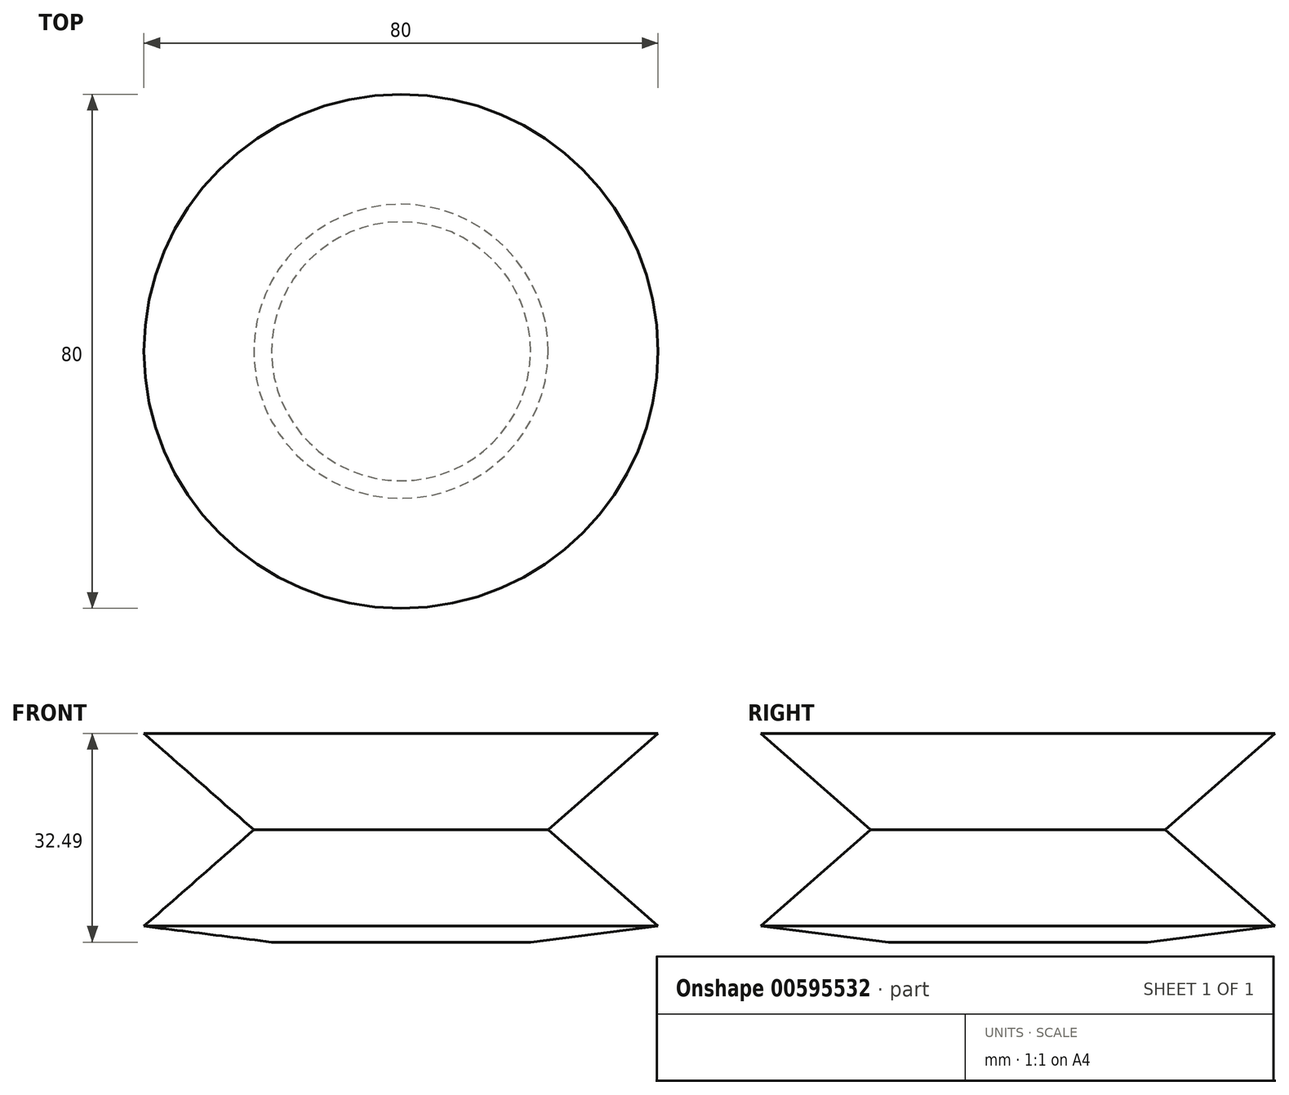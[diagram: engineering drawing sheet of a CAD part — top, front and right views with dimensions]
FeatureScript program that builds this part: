
annotation { "Feature Type Name" : "Feature", "Feature Type Description" : "" }
export const myFeature = defineFeature(function(context is Context, id is Id, definition is map)
    precondition{}
    {
        {
            var Q0;
            Q0=qCreatedBy(makeId("Front.planeOp"),FACE);
            var sketch = newSketch(context, id + "F0", { "sketchPlane" : qUnion([Q0])});
            skLineSegment(sketch, "E0", {"start": v(0, 0) * mm, "end": v(0, 32.49) * mm});
            skLineSegment(sketch, "E1", {"start": v(0, 32.49) * mm, "end": v(40, 32.49) * mm});
            skLineSegment(sketch, "E2", {"start": v(40, 32.49) * mm, "end": v(22.9, 17.49) * mm});
            skLineSegment(sketch, "E3", {"start": v(22.9, 17.49) * mm, "end": v(40, 2.49) * mm});
            skLineSegment(sketch, "E4", {"start": v(40, 2.49) * mm, "end": v(20.16, 0) * mm});
            skLineSegment(sketch, "E5", {"start": v(20.16, 0) * mm, "end": v(0, 0) * mm});
            skSolve(sketch);
        }
        {
            var Q0;
            Q0=makeQuery(id+"F0.imprint","IMPRINT",FACE,{"disambiguationData":[TD([[makeQuery(id+"F0.imprint","IMPRINT",EDGE,{"derivedFrom":sQuery(id+"F0.wireOp",EDGE,"E0")}),-1.0]])]});
            var Q1;
            Q1=sQuery(id+"F0.wireOp",EDGE,"E0");
            revolve(context, id + "F1", {"entities" : qUnion([Q0]), "axis" : qUnion([Q1]), "revolveType" : RevolveType.FULL});
        }
    });
